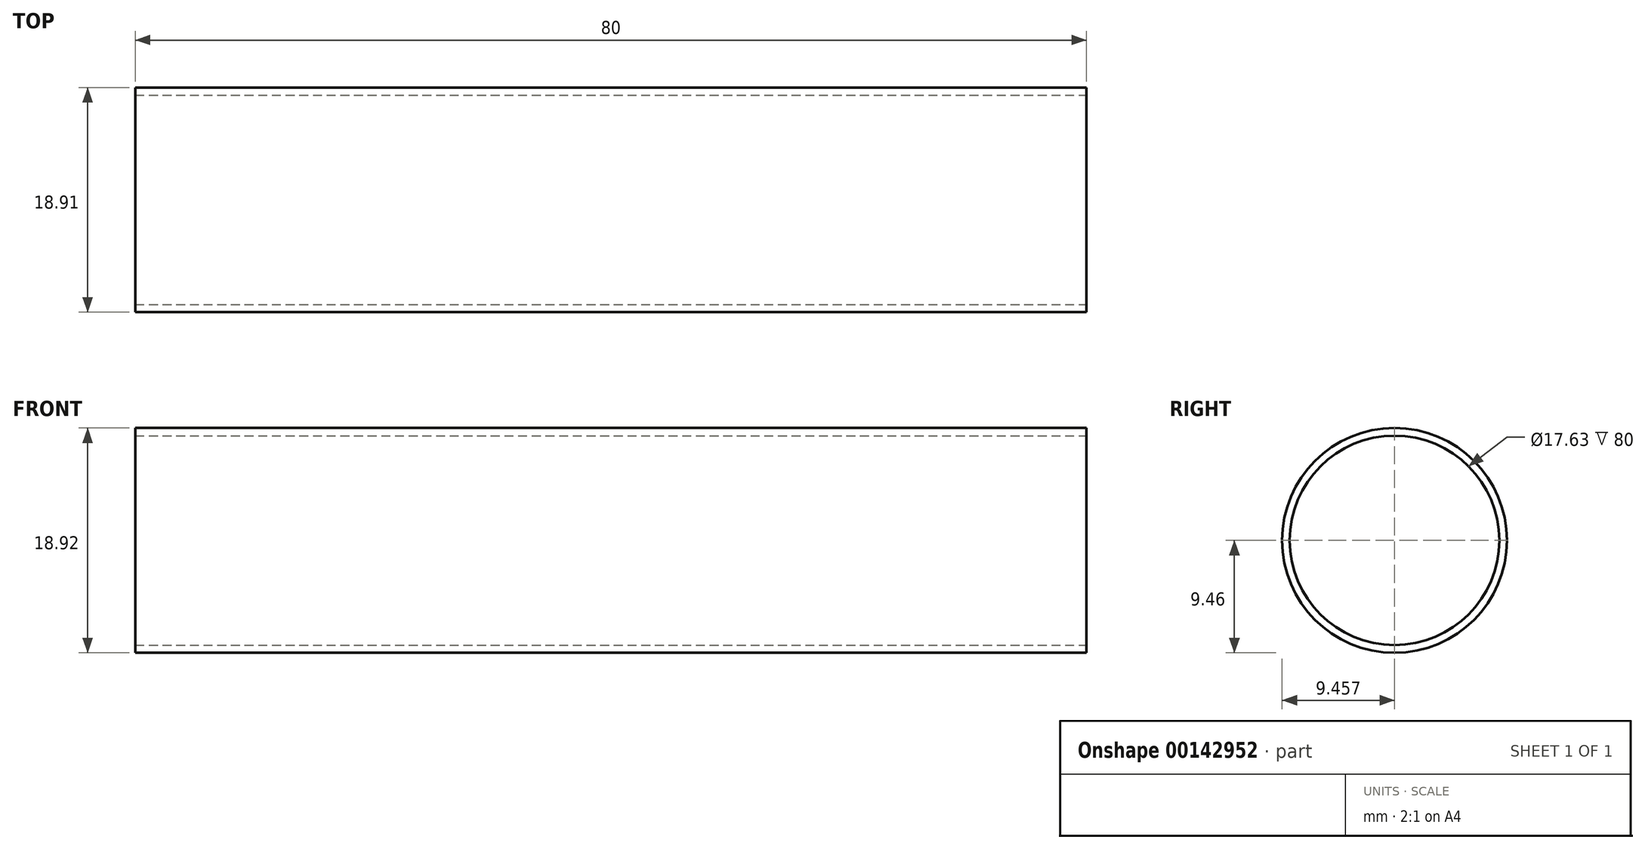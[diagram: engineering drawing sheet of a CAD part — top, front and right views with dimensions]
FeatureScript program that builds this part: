
annotation { "Feature Type Name" : "Feature", "Feature Type Description" : "" }
export const myFeature = defineFeature(function(context is Context, id is Id, definition is map)
    precondition{}
    {
        {
            var Q0;
            Q0=qCreatedBy(makeId("Right.planeOp"),FACE);
            var sketch = newSketch(context, id + "F0", { "sketchPlane" : qUnion([Q0])});
            skCircle(sketch, "E0", {"center": v(-10.85, 0) * mm, "radius": 9.46 * mm});
            skSolve(sketch);
        }
        {
            var Q0;
            Q0=makeQuery(id+"F0.imprint","IMPRINT",FACE,{"disambiguationData":[TD([[makeQuery(id+"F0.imprint","IMPRINT",EDGE,{"derivedFrom":sQuery(id+"F0.wireOp",EDGE,"E0")}),1.0]])]});
            extrude(context, id + "F1", {"entities" : qUnion([Q0]), "depth" : 80 * mm});
        }
        {
            var Q0;
            Q0=makeQuery(id+"F1.opExtrude","CAP_FACE",FACE,{"disambiguationData":[OSD([sQuery(id+"F0.wireOp",EDGE,"E0")])],"isStart":false});
            var sketch = newSketch(context, id + "F2", { "sketchPlane" : qUnion([Q0])});
            skCircle(sketch, "E1", {"center": v(-10.85, 0) * mm, "radius": 8.8 * mm});
            skSolve(sketch);
        }
        {
            var Q0;
            Q0=sQuery(id+"F2.wireOp",VERTEX,"E1.center");
            var Q1;
            Q1=makeQuery(id+"F1.opExtrude","SWEPT_BODY",BODY,{"disambiguationData":[OSD([sQuery(id+"F0.wireOp",EDGE,"E0")])]});
            hole(context, id + "F3", {"style" : HoleStyle.C_BORE, "endStyle" : HoleEndStyle.THROUGH, "holeDiameter" : 17.63 * mm, "cBoreDiameter" : 17.63 * mm, "cBoreDepth" : 80 * mm, "startFromSketch" : true, "locations" : qUnion([Q0]), "scope" : qUnion([Q1]), "isTappedThrough" : true});
        }
        {
            var Q0;
            Q0=sQuery(id+"F2.wireOp",EDGE,"E1");
            var Q1;
            Q1=sQuery(id+"F0.wireOp",EDGE,"E0");
            extrude(context, id + "F4", {"bodyType" : ToolBodyType.SURFACE, "surfaceEntities" : qUnion([Q0, Q1]), "depth" : 20 * mm});
        }
    });
